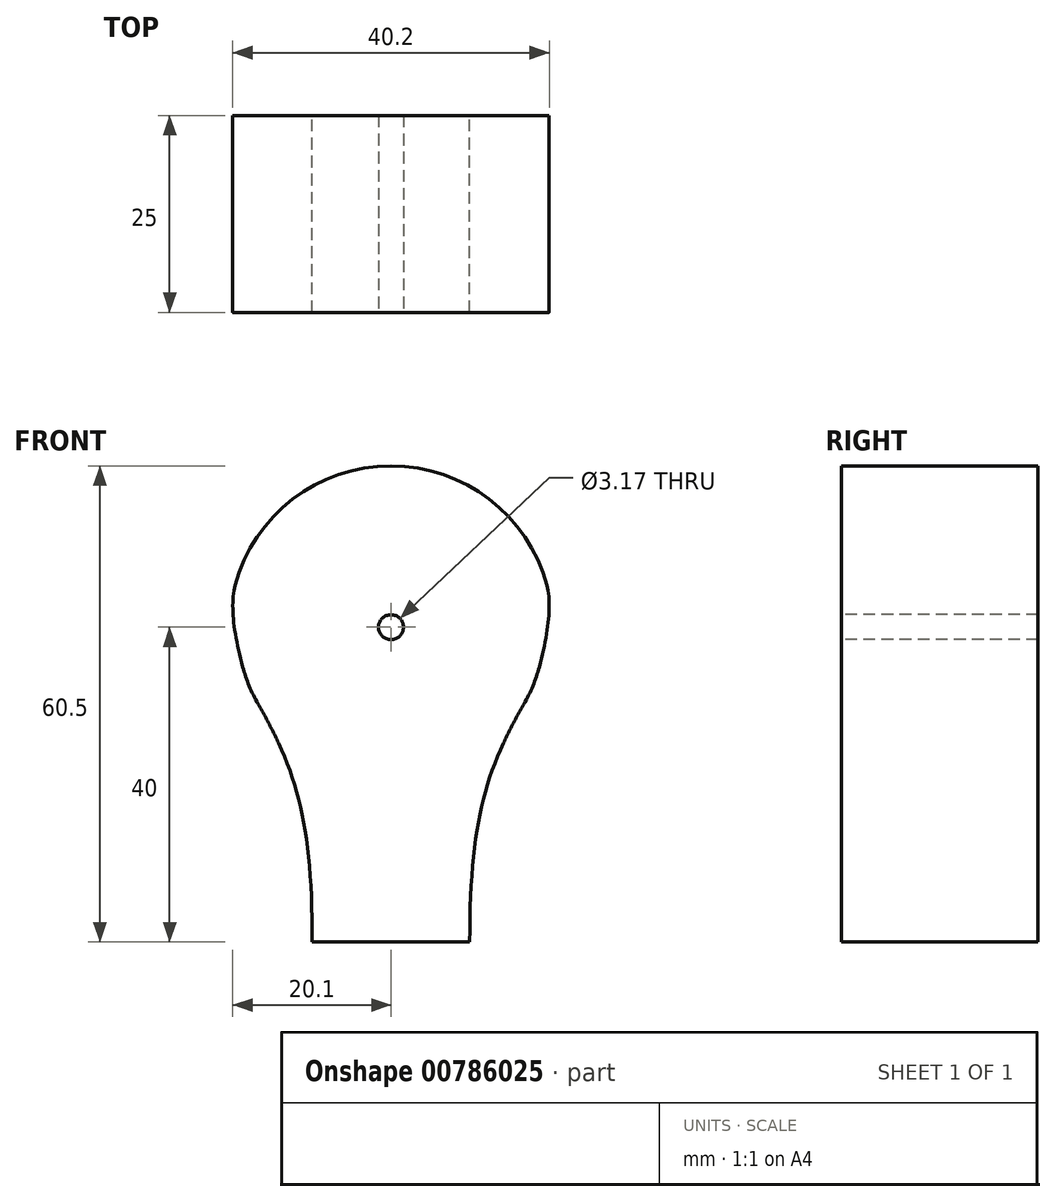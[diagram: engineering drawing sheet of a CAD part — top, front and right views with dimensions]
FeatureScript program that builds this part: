
annotation { "Feature Type Name" : "Feature", "Feature Type Description" : "" }
export const myFeature = defineFeature(function(context is Context, id is Id, definition is map)
    precondition{}
    {
        {
            var Q0;
            Q0=qCreatedBy(makeId("Front.planeOp"),FACE);
            var sketch = newSketch(context, id + "F0", { "sketchPlane" : qUnion([Q0])});
            skLineSegment(sketch, "E0.bottom", {"start": v(10, 0) * mm, "end": v(-10, 0) * mm, "construction": true});
            skLineSegment(sketch, "E0.top", {"start": v(10, -40) * mm, "end": v(-10, -40) * mm});
            skLineSegment(sketch, "E0.left", {"start": v(10, 0) * mm, "end": v(10, -40) * mm, "construction": true});
            skLineSegment(sketch, "E0.right", {"start": v(-10, 0) * mm, "end": v(-10, -40) * mm, "construction": true});
            skPoint(sketch, "E0.middle", {"position": v(0, -20) * mm});
            skCircle(sketch, "E1", {"center": v(0, 0) * mm, "radius": 19.5 * mm});
            skCircle(sketch, "E2", {"center": v(0, 0) * mm, "radius": 20.5 * mm});
            skLineSegment(sketch, "E3", {"start": v(0, 0) * mm, "end": v(19.8, 5.3) * mm, "construction": true});
            skLineSegment(sketch, "E4", {"start": v(0, 0) * mm, "end": v(18.84, -5.05) * mm, "construction": true});
            skLineSegment(sketch, "E5", {"start": v(0, 0) * mm, "end": v(16.89, -9.75) * mm, "construction": true});
            skLineSegment(sketch, "E6", {"start": v(0, 0) * mm, "end": v(17.75, 10.25) * mm, "construction": true});
            skLineSegment(sketch, "E7", {"start": v(19.8, 5.3) * mm, "end": v(19.8, 5.3) * mm});
            skLineSegment(sketch, "E8", {"start": v(16.89, -9.75) * mm, "end": v(11.89, -18.41) * mm});
            skLineSegment(sketch, "E9", {"start": v(0, -40) * mm, "end": v(0, 20.5) * mm, "construction": true});
            skFitSpline(sketch, "E10.MirrorCS", {"points": [v(-16.89, -9.75) * mm, v(-10, -40) * mm], "startDerivative": vector(15, -25.98) * mm, "endDerivative": vector(0, -45) * mm});
            skLineSegment(sketch, "E11.MirrorCS", {"start": v(0, 0) * mm, "end": v(-17.75, 10.25) * mm});
            skFitSpline(sketch, "E12", {"points": [v(19.8, 5.3) * mm, v(18.84, -5.05) * mm], "startDerivative": vector(1.96, -7.3) * mm, "endDerivative": vector(-3.42, -12.77) * mm});
            skLineSegment(sketch, "E13", {"start": v(19.8, 5.3) * mm, "end": v(20.45, 2.87) * mm, "construction": true});
            skLineSegment(sketch, "E14", {"start": v(18.84, -5.05) * mm, "end": v(19.98, -0.79) * mm, "construction": true});
            skLineSegment(sketch, "E15.MirrorCS", {"start": v(0, 0) * mm, "end": v(-17.75, 10.25) * mm, "construction": true});
            skLineSegment(sketch, "E16.MirrorCS", {"start": v(0, 0) * mm, "end": v(-19.8, 5.3) * mm, "construction": true});
            skLineSegment(sketch, "E17.MirrorCS", {"start": v(0, 0) * mm, "end": v(-18.84, -5.05) * mm, "construction": true});
            skLineSegment(sketch, "E18.MirrorCS", {"start": v(0, 0) * mm, "end": v(-16.89, -9.75) * mm, "construction": true});
            skFitSpline(sketch, "E19.MirrorCS", {"points": [v(-19.8, 5.3) * mm, v(-18.84, -5.05) * mm], "startDerivative": vector(-1.96, -7.3) * mm, "endDerivative": vector(3.42, -12.77) * mm});
            skFitSpline(sketch, "E20.MirrorCS", {"points": [v(16.89, -9.75) * mm, v(10, -40) * mm], "startDerivative": vector(-15, -25.98) * mm, "endDerivative": vector(0, -45) * mm});
            skSolve(sketch);
        }
        {
            var Q0;
            {var subQ0=sQuery(id+"F0.wireOp",EDGE,"E19.MirrorCS");Q0=makeQuery(id+"F0.imprint","IMPRINT",FACE,{"disambiguationData":[TD([[makeQuery(id+"F0.imprint","IMPRINT",EDGE,{"derivedFrom":subQ0}),1.0]])]});}
            var Q1;
            {var subQ0=sQuery(id+"F0.wireOp",EDGE,"E12");Q1=makeQuery(id+"F0.imprint","IMPRINT",FACE,{"disambiguationData":[TD([[makeQuery(id+"F0.imprint","IMPRINT",EDGE,{"derivedFrom":subQ0}),-1.0]])]});}
            var Q2;
            {var subQ0=sQuery(id+"F0.wireOp",EDGE,"E1");var subQ4=makeQuery(id+"F0.imprint","INTERSECT",VERTEX,{"derivedFrom":[subQ0,sQuery(id+"F0.wireOp",EDGE,"E19.MirrorCS")]});Q2=makeQuery(id+"F0.imprint","IMPRINT",FACE,{"disambiguationData":[TD([[makeQuery(id+"F0.imprint","IMPRINT",EDGE,{"disambiguationData":[TD([[subQ4,1.0]])],"derivedFrom":subQ0}),1.0]])]});}
            var Q3;
            {var subQ3=sQuery(id+"F0.wireOp",EDGE,"E10.MirrorCS");var subQ5=sQuery(id+"F0.wireOp",EDGE,"E2");var subQ6=makeQuery(id+"F0.imprint","INTERSECT",VERTEX,{"derivedFrom":[subQ5,subQ3]});Q3=makeQuery(id+"F0.imprint","IMPRINT",FACE,{"disambiguationData":[TD([[makeQuery(id+"F0.imprint","IMPRINT",EDGE,{"disambiguationData":[TD([[subQ6,-1.0]])],"derivedFrom":subQ5}),1.0]])]});}
            var Q4;
            {var subQ1=sQuery(id+"F0.wireOp",EDGE,"E0.top");Q4=makeQuery(id+"F0.imprint","IMPRINT",FACE,{"disambiguationData":[TD([[makeQuery(id+"F0.imprint","IMPRINT",EDGE,{"derivedFrom":subQ1}),-1.0]])]});}
            var Q5;
            {var subQ0=sQuery(id+"F0.wireOp",EDGE,"E8");var subQ1=sQuery(id+"F0.wireOp",EDGE,"E2");var subQ2=makeQuery(id+"F0.imprint","INTERSECT",VERTEX,{"derivedFrom":[subQ1,subQ0]});Q5=makeQuery(id+"F0.imprint","IMPRINT",FACE,{"disambiguationData":[TD([[makeQuery(id+"F0.imprint","IMPRINT",EDGE,{"disambiguationData":[TD([[subQ2,-1.0]])],"derivedFrom":subQ1}),1.0]])]});}
            extrude(context, id + "F1", {"entities" : qUnion([Q0, Q1, Q2, Q3, Q4, Q5]), "depth" : 25 * mm, "offsetDistance" : 25 * mm});
        }
        {
            var Q0;
            Q0=makeQuery(id+"F1.opExtrude","CAP_FACE",FACE,{"disambiguationData":[OSD([sQuery(id+"F0.wireOp",EDGE,"E0.top"),sQuery(id+"F0.wireOp",EDGE,"E1"),sQuery(id+"F0.wireOp",EDGE,"E2"),sQuery(id+"F0.wireOp",EDGE,"7a9026b3-197f-48e2-9b81-13cee80a4807"),sQuery(id+"F0.wireOp",EDGE,"0a668d27-42bc-4e6d-9f5e-2706f69a0711"),sQuery(id+"F0.wireOp",EDGE,"f3387c69-d86e-4529-9347-0b486354b344.MirrorCS"),sQuery(id+"F0.wireOp",EDGE,"E10.MirrorCS")])],"isStart":false});
            var sketch = newSketch(context, id + "F2", { "sketchPlane" : qUnion([Q0])});
            skCircle(sketch, "E21", {"center": v(0, 0) * mm, "radius": 1.59 * mm});
            skSolve(sketch);
        }
        {
            var Q0;
            Q0=qSketchRegion(id+"F2",true);
            extrude(context, id + "F3", {"entities" : qUnion([Q0]), "operationType" : NewBodyOperationType.REMOVE, "oppositeDirection" : true, "depth" : 25 * mm, "offsetDistance" : 25 * mm});
        }
    });
